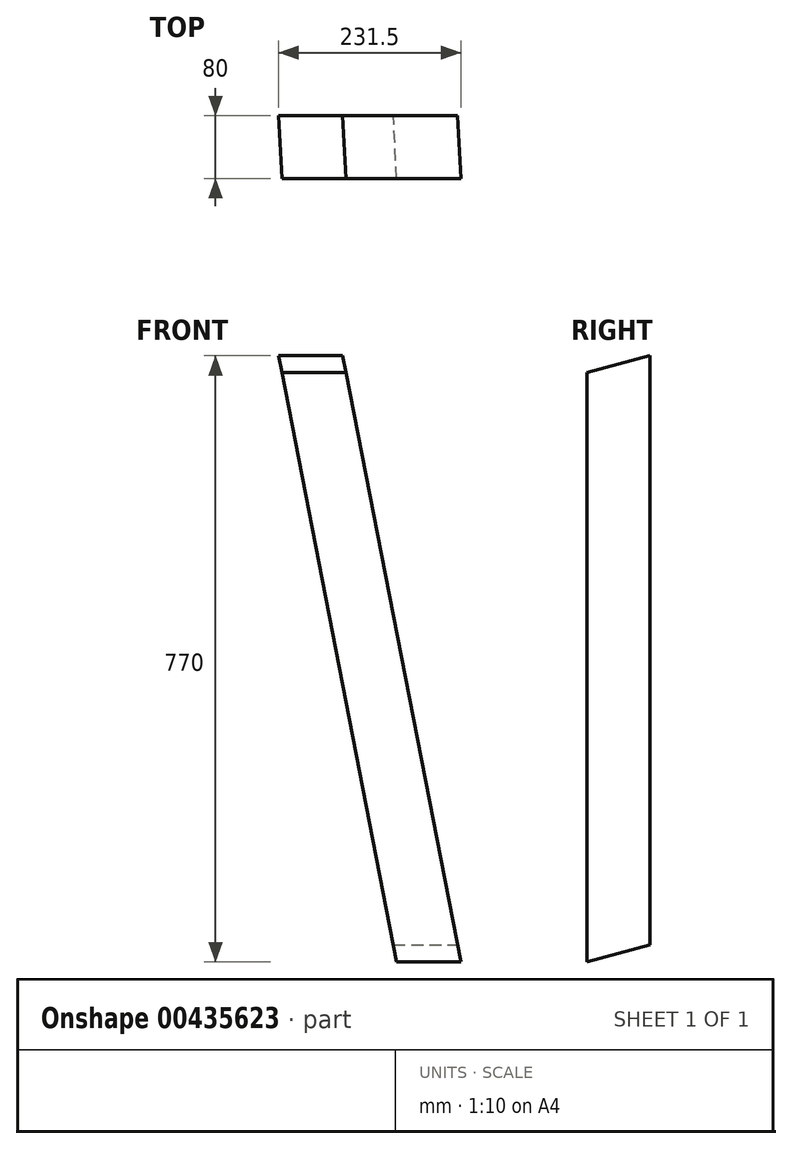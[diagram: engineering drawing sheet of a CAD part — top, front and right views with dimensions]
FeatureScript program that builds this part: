
annotation { "Feature Type Name" : "Feature", "Feature Type Description" : "" }
export const myFeature = defineFeature(function(context is Context, id is Id, definition is map)
    precondition{}
    {
        {
            var Q0;
            Q0=qCreatedBy(makeId("Front.planeOp"),FACE);
            var sketch = newSketch(context, id + "F0", { "sketchPlane" : qUnion([Q0])});
            skLineSegment(sketch, "E0", {"start": v(0, 0) * mm, "end": v(0, 770) * mm, "construction": true});
            skLineSegment(sketch, "E1", {"start": v(0, 770) * mm, "end": v(-150, 770) * mm, "construction": true});
            skLineSegment(sketch, "E2", {"start": v(-150, 770) * mm, "end": v(0, 0) * mm});
            skLineSegment(sketch, "E3", {"start": v(-6.37, 32.7) * mm, "end": v(-84.9, 17.4) * mm, "construction": true});
            skLineSegment(sketch, "E4", {"start": v(-84.9, 17.4) * mm, "end": v(-231.5, 770) * mm});
            skLineSegment(sketch, "E5", {"start": v(-84.9, 17.4) * mm, "end": v(-81.5, 0) * mm});
            skLineSegment(sketch, "E6", {"start": v(-81.5, 0) * mm, "end": v(0, 0) * mm});
            skLineSegment(sketch, "E7", {"start": v(-150, 770) * mm, "end": v(-231.5, 770) * mm});
            skSolve(sketch);
        }
        {
            var Q0;
            Q0 = qSketchRegion(id + "F0", true);
            extrude(context, id + "F1", {"entities" : qUnion([Q0]), "oppositeDirection" : true, "depth" : 80 * mm});
        }
        {
            var Q0;
            Q0=qCreatedBy(makeId("Right.planeOp"),FACE);
            var sketch = newSketch(context, id + "F2", { "sketchPlane" : qUnion([Q0])});
            skLineSegment(sketch, "E8", {"start": v(0, 0) * mm, "end": v(247.9, 0) * mm, "construction": true});
            skLineSegment(sketch, "E9", {"start": v(0, 0) * mm, "end": v(116.67, 31.26) * mm});
            skLineSegment(sketch, "E10", {"start": v(116.67, 31.26) * mm, "end": v(116.67, 0) * mm});
            skLineSegment(sketch, "E11", {"start": v(116.67, 0) * mm, "end": v(0, 0) * mm});
            skLineSegment(sketch, "E12", {"start": v(0, 0) * mm, "end": v(0, 770) * mm, "construction": true});
            skLineSegment(sketch, "E13", {"start": v(0, 770) * mm, "end": v(80, 770) * mm, "construction": true});
            skLineSegment(sketch, "E14", {"start": v(80, 770) * mm, "end": v(-37.18, 738.6) * mm});
            skLineSegment(sketch, "E15", {"start": v(-37.18, 738.6) * mm, "end": v(-37.18, 770) * mm});
            skLineSegment(sketch, "E16", {"start": v(-37.18, 770) * mm, "end": v(80, 770) * mm});
            skSolve(sketch);
        }
        {
            var Q0;
            Q0 = qSketchRegion(id + "F2", true);
            extrude(context, id + "F3", {"entities" : qUnion([Q0]), "operationType" : NewBodyOperationType.REMOVE, "oppositeDirection" : true, "depth" : 300 * mm});
        }
    });
